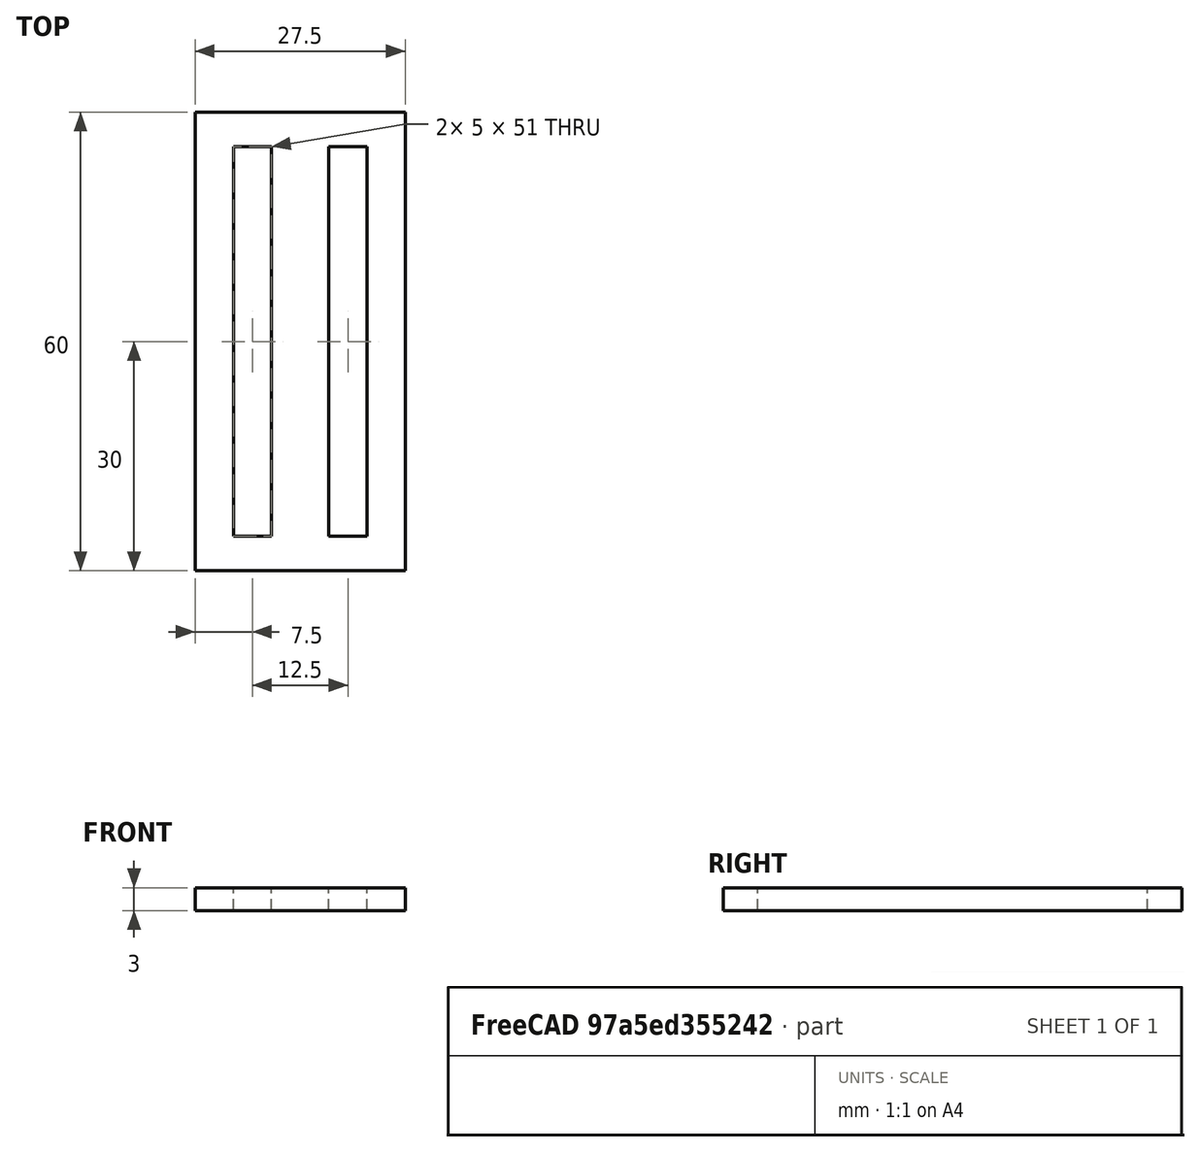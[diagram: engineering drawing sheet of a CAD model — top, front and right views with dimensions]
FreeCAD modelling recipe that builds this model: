
FCSTD DOCUMENT  (FreeCAD 0.21R33694 (Git))
Label: StrapHolder
License: All rights reserved
LicenseURL: https://en.wikipedia.org/wiki/All_rights_reserved
objects: Sketcher::SketchObject×1, PartDesign::Pad×1, PartDesign::Body×1
note: 4 computed .brp shape members not serialized (recipe doc carries the construction recipe); baked Part::Feature solids carry a one-line shape summary decoded from their .brp

FEATURE [Sketcher::SketchObject] Sketch  label="BaseSketch"
  FullyConstrained = true
  MapMode = 5
  Support = -> [XY_Plane]
  sketch-geometry (15):
    g0: LineSegment StartX=-13.75 StartY=-30 StartZ=0 EndX=-13.75 EndY=30 EndZ=0
    g1: LineSegment StartX=-13.75 StartY=30 StartZ=0 EndX=13.75 EndY=30 EndZ=0
    g2: LineSegment StartX=13.75 StartY=30 StartZ=0 EndX=13.75 EndY=-30 EndZ=0
    g3: LineSegment StartX=13.75 StartY=-30 StartZ=0 EndX=-13.75 EndY=-30 EndZ=0
    g4: GeomPoint X=0 Y=0 Z=0
    g5: LineSegment StartX=-8.75 StartY=-25.5 StartZ=0 EndX=-8.75 EndY=25.5 EndZ=0
    g6: LineSegment StartX=-8.75 StartY=25.5 StartZ=0 EndX=-3.75 EndY=25.5 EndZ=0
    g7: LineSegment StartX=-3.75 StartY=25.5 StartZ=0 EndX=-3.75 EndY=-25.5 EndZ=0
    g8: LineSegment StartX=-3.75 StartY=-25.5 StartZ=0 EndX=-8.75 EndY=-25.5 EndZ=0
    g9: GeomPoint X=-6.25 Y=0 Z=0
    g10: LineSegment StartX=3.75 StartY=-25.5 StartZ=0 EndX=3.75 EndY=25.5 EndZ=0
    g11: LineSegment StartX=3.75 StartY=25.5 StartZ=0 EndX=8.75 EndY=25.5 EndZ=0
    g12: LineSegment StartX=8.75 StartY=25.5 StartZ=0 EndX=8.75 EndY=-25.5 EndZ=0
    g13: LineSegment StartX=8.75 StartY=-25.5 StartZ=0 EndX=3.75 EndY=-25.5 EndZ=0
    g14: GeomPoint X=6.25 Y=0 Z=0
  constraints (37):
    c: Coincident(g0,g1)
    c: Coincident(g1,g2)
    c: Coincident(g2,g3)
    c: Coincident(g3,g0)
    c: Horizontal(g1)
    c: Horizontal(g3)
    c: Vertical(g0)
    c: Vertical(g2)
    c: Symmetric(g1,g0,g4)
    c: Coincident(g4,g-1)
    c: DistanceY(g2,g2) = 60
    c: Coincident(g5,g6)
    c: Coincident(g6,g7)
    c: Coincident(g7,g8)
    c: Coincident(g8,g5)
    c: Horizontal(g6)
    c: Horizontal(g8)
    c: Vertical(g5)
    c: Vertical(g7)
    c: Symmetric(g6,g5,g9)
    c: PointOnObject(g9,g-1)
    c: Coincident(g10,g11)
    c: Coincident(g11,g12)
    c: Coincident(g12,g13)
    c: Coincident(g13,g10)
    c: Horizontal(g11)
    c: Horizontal(g13)
    c: Vertical(g10)
    c: Vertical(g12)
    c: Symmetric(g11,g10,g14)
    c: PointOnObject(g14,g-1)
    c: DistanceX(g11,g11) = 5
    c: DistanceX(g6,g6) = 5
    c: Distance(g6,g10) = 7.5
    c: Symmetric(g10,g7,g4)
    c: DistanceX(g1,g1) = 27.5
    c: DistanceY(g5,g5) = 51
FEATURE [PartDesign::Pad] Pad  label="Base"
  Direction = (0,0,1)
  Length = 3
  Length2 = 10
  Profile = -> Sketch
  ReferenceAxis = -> Sketch [N_Axis]
  Type = 0
FEATURE [PartDesign::Body] Body
  Group = -> [Sketch,Pad]
  Origin = -> Origin
  Tip = -> Pad
